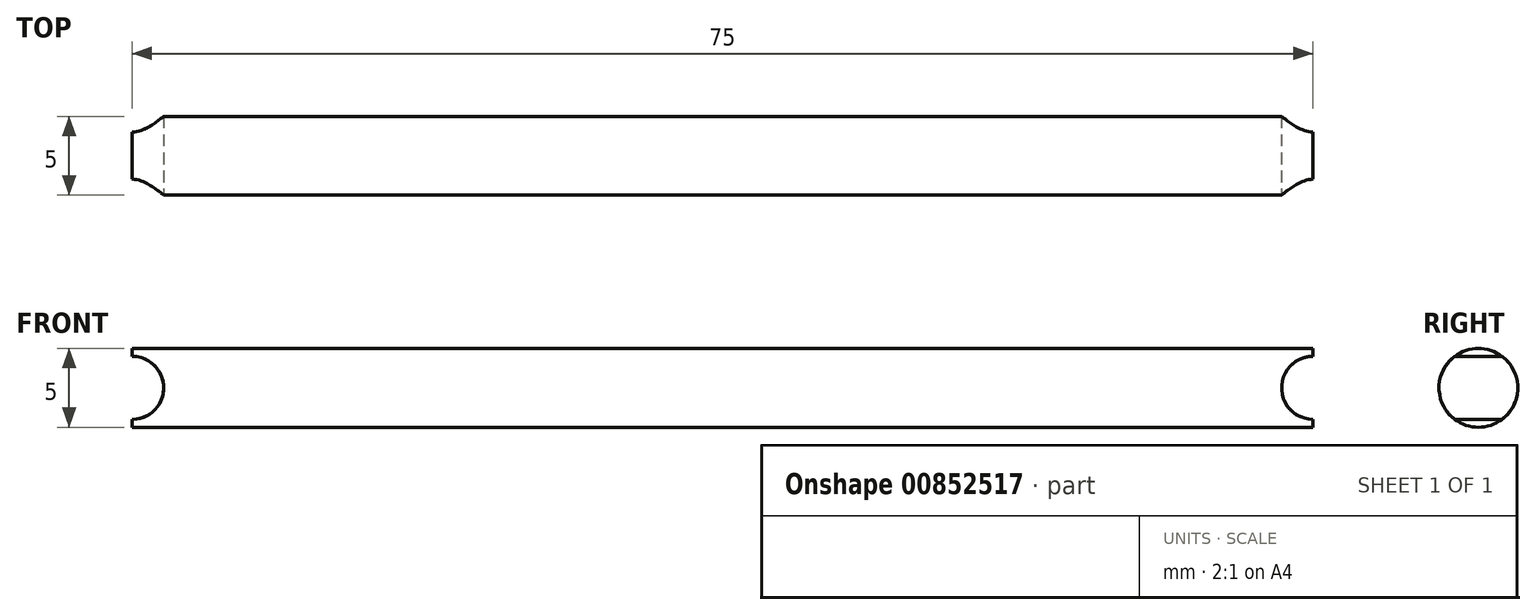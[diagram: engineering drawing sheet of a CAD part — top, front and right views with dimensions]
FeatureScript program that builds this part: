
annotation { "Feature Type Name" : "Feature", "Feature Type Description" : "" }
export const myFeature = defineFeature(function(context is Context, id is Id, definition is map)
    precondition{}
    {
        {
            assignVariable(context, id + "F0", {"name" : "RodLength", "anyValue" : 75});
        }
        {
            var Q0;
            Q0=qCreatedBy(makeId("Right.planeOp"),FACE);
            var sketch = newSketch(context, id + "F1", { "sketchPlane" : qUnion([Q0])});
            skCircle(sketch, "E0", {"center": v(0, 0) * mm, "radius": 2.5 * mm});
            skSolve(sketch);
        }
        {
            var Q0;
            Q0=qSketchRegion(id+"F1",true);
            extrude(context, id + "F2", {"entities" : qUnion([Q0]), "endBound" : BoundingType.SYMMETRIC, "depth" : (getVariable(context, 'RodLength')) * mm, "offsetDistance" : 25 * mm});
        }
        {
            var Q0;
            Q0=qCreatedBy(makeId("Front.planeOp"),FACE);
            var sketch = newSketch(context, id + "F3", { "sketchPlane" : qUnion([Q0])});
            skLineSegment(sketch, "E1.0", {"start": v(-37.5, 2.5) * mm, "end": v(-37.5, -2.5) * mm, "construction": true});
            skPoint(sketch, "E2", {"position": v(-37.5, 0) * mm});
            skCircle(sketch, "E3", {"center": v(-37.5, 0) * mm, "radius": 2 * mm});
            skCircle(sketch, "E4.MirrorC", {"center": v(37.5, 0) * mm, "radius": 2 * mm});
            skSolve(sketch);
        }
        {
            var Q0;
            Q0=qSketchRegion(id+"F3",true);
            extrude(context, id + "F4", {"entities" : qUnion([Q0]), "operationType" : NewBodyOperationType.REMOVE, "endBound" : BoundingType.THROUGH_ALL, "oppositeDirection" : true, "depth" : 25 * mm, "offsetDistance" : 25 * mm, "hasSecondDirection" : true, "secondDirectionBound" : SecondDirectionBoundingType.THROUGH_ALL, "secondDirectionOppositeDirection" : false, "secondDirectionDepth" : 25 * mm});
        }
    });
